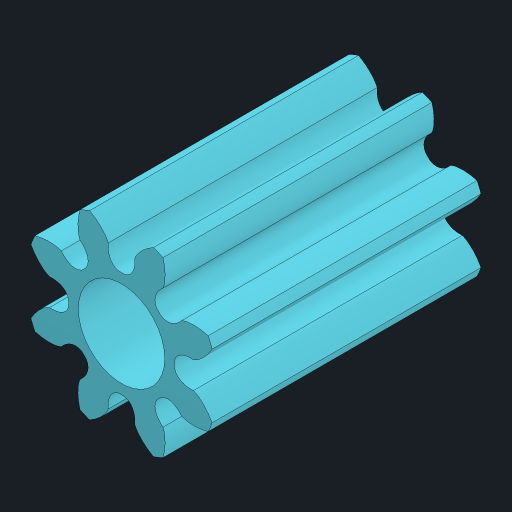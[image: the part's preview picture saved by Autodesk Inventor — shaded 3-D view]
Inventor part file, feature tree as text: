
AUTODESK INVENTOR PART (.ipt)
format: ipt  version: 2023.2 (Build 272271030, 271C)  size: 489,472 bytes
history: native  units: mm
features: sketch x2, extrude x2, pattern_circular x1, hole x1
ambient origin geometry x8: Origin, YZ Plane, XZ Plane, XY Plane, X Axis, Y Axis, Z Axis, Center Point
bodies: Solid1 (feature_tree)
feature tree (6):
  sketch  "Sketch1"  dims[d0=14.0mm d1=0.0mm d2=0.0mm d3=0.0mm]
  extrude  "Extrusion1"  TaperAngle=0.0deg  [1 undecoded]
  extrude  "Extrusion2"  TaperAngle=0.0deg  [1 undecoded]
  pattern_circular  "Circular Pattern1"  [2 undecoded]
  hole  "Hole1"  [1 undecoded]
  sketch  "Sketch2"  dims[d4=80.0mm d5=360.0deg d7=2.5mm d8=6.0mm d9=4.5mm d10=5.8mm d11=90.0deg d12=8.0mm d13=20.594885mm d17=0.0mm d18=0.0mm d19=0.0mm d20=0.0mm]
note: 5 required parameter values undecoded (feature->parameter linkage not recoverable at this tier; creation-order binding heuristic only, values carry confidence <= 0.55)
